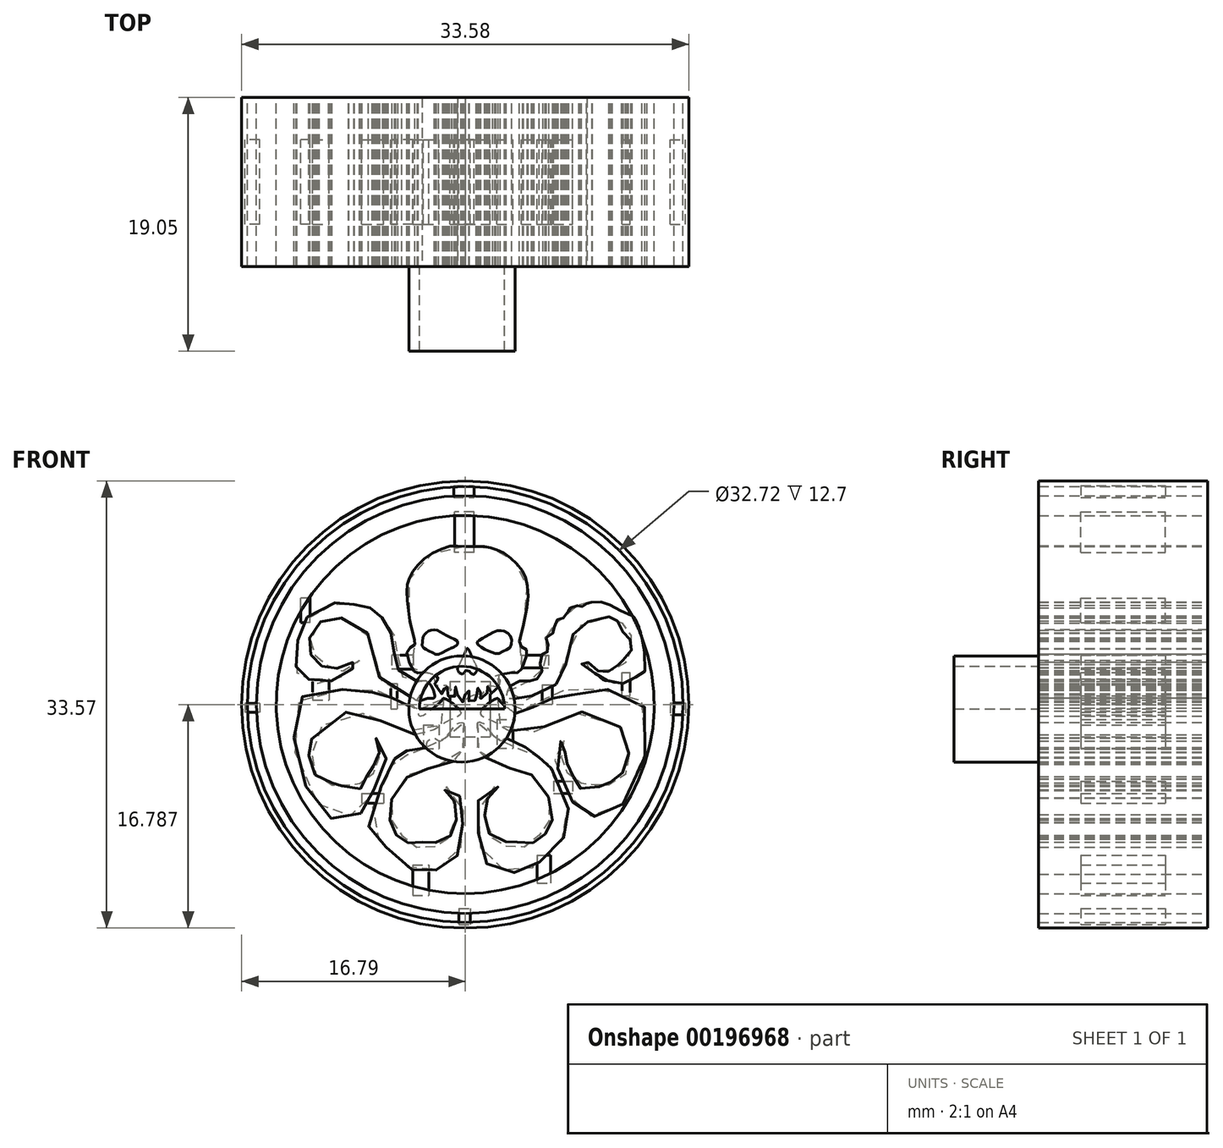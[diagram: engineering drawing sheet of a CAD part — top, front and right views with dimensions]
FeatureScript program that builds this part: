
annotation { "Feature Type Name" : "Feature", "Feature Type Description" : "" }
export const myFeature = defineFeature(function(context is Context, id is Id, definition is map)
    precondition{}
    {
        {
            var Q0;
            Q0=qCreatedBy(makeId("Front.planeOp"),FACE);
            var sketch = newSketch(context, id + "F0", { "sketchPlane" : qUnion([Q0])});
            skCircle(sketch, "E0", {"center": v(0.24, 0.34) * mm, "radius": 14.2 * mm});
            skCircle(sketch, "E1", {"center": v(0.24, 0.34) * mm, "radius": 15.68 * mm});
            skCircle(sketch, "E2", {"center": v(0.24, 0.34) * mm, "radius": 16.79 * mm});
            skCircle(sketch, "E3", {"center": v(0.24, 0.34) * mm, "radius": 16.36 * mm});
            skFitSpline(sketch, "E4", {"points": [v(0.24, 12.2) * mm, v(-0.86, 12.23) * mm, v(-2.49, 11.52) * mm, v(-3.6, 10.47) * mm, v(-4.06, 9.5) * mm, v(-4.12, 8.58) * mm, v(-3.9, 6.56) * mm, v(-3.64, 5.47) * mm, v(-3.58, 5.15) * mm, v(-3.58, 4.8) * mm, v(-4.12, 4.38) * mm, v(-3.55, 2.78) * mm, v(-3.29, 2.72) * mm, v(-2.58, 2.72) * mm, v(-2.06, 2.57) * mm, v(-1.85, 2.46) * mm, v(-1.75, 2.3) * mm, v(-2.04, 2.17) * mm, v(-1.82, 1.47) * mm, v(-1.34, 1.12) * mm, v(-1.27, 1.79) * mm, v(-1.14, 1.72) * mm, v(-1.11, 1.08) * mm, v(-0.58, 0.8) * mm, v(-0.56, 1.6) * mm, v(-0.35, 1.63) * mm, v(-0.33, 0.8) * mm, v(0.24, 0.58) * mm, v(0.24, 1.37) * mm, v(0.53, 1.37) * mm, v(0.53, 0.58) * mm, v(0.7, 0.58) * mm, v(1.14, 0.72) * mm, v(1.11, 1.02) * mm, v(1.14, 1.53) * mm, v(1.36, 1.57) * mm, v(1.38, 1.29) * mm, v(1.34, 0.8) * mm, v(1.84, 1.04) * mm, v(1.88, 1.47) * mm, v(1.92, 1.69) * mm, v(2.06, 1.77) * mm, v(2.02, 1.23) * mm, v(2.14, 1.16) * mm, v(2.55, 1.37) * mm, v(2.84, 2.2) * mm, v(2.53, 2.23) * mm, v(2.47, 2.38) * mm, v(2.6, 2.5) * mm, v(3.76, 2.74) * mm, v(4.1, 2.72) * mm, v(4.36, 2.79) * mm, v(4.9, 4.41) * mm, v(4.79, 4.45) * mm, v(4.38, 4.8) * mm, v(4.32, 5.16) * mm, v(4.5, 5.89) * mm, v(4.7, 6.75) * mm, v(4.95, 8.35) * mm, v(4.87, 9.56) * mm, v(4.58, 10.28) * mm, v(4, 11.03) * mm, v(3.25, 11.63) * mm, v(2.63, 11.96) * mm, v(2.06, 12.12) * mm, v(1.5, 12.2) * mm, v(0.24, 12.2) * mm]});
            skFitSpline(sketch, "E5", {"points": [v(-0.33, 5.1) * mm, v(-0.8, 5.34) * mm, v(-1.34, 5.62) * mm, v(-1.6, 5.78) * mm, v(-1.92, 5.92) * mm, v(-2.27, 5.94) * mm, v(-2.53, 5.84) * mm, v(-2.7, 5.7) * mm, v(-2.87, 5.5) * mm, v(-2.96, 5.2) * mm, v(-2.96, 4.65) * mm, v(-2.81, 4.55) * mm, v(-2.6, 4.43) * mm, v(-2.13, 4.19) * mm, v(-1.88, 4.09) * mm, v(-1.38, 4.27) * mm, v(-0.94, 4.53) * mm], "startDerivative": vector(-5.86, 3.13) * mm, "endDerivative": vector(5.52, 3.48) * mm});
            skFitSpline(sketch, "E6", {"points": [v(-0.94, 4.53) * mm, v(-0.7, 4.62) * mm, v(-0.43, 4.77) * mm, v(-0.34, 4.89) * mm, v(-0.33, 4.99) * mm, v(-0.33, 5.1) * mm], "startDerivative": vector(0.91, 0.3) * mm, "endDerivative": vector(0, 0.7) * mm});
            skFitSpline(sketch, "E7", {"points": [v(2.95, 5.9) * mm, v(2.67, 5.89) * mm, v(2.37, 5.75) * mm, v(2.08, 5.62) * mm, v(1.8, 5.46) * mm, v(1.6, 5.34) * mm, v(1.4, 5.23) * mm, v(1.23, 5.1) * mm, v(1.14, 5.04) * mm, v(1.14, 4.9) * mm, v(1.25, 4.8) * mm, v(1.48, 4.62) * mm, v(1.72, 4.47) * mm, v(1.97, 4.37) * mm, v(2.2, 4.3) * mm, v(2.43, 4.21) * mm, v(2.6, 4.14) * mm, v(2.86, 4.2) * mm, v(3.16, 4.36) * mm, v(3.45, 4.5) * mm, v(3.63, 4.65) * mm, v(3.7, 4.82) * mm, v(3.72, 5.12) * mm, v(3.68, 5.42) * mm, v(3.53, 5.6) * mm, v(3.33, 5.78) * mm, v(3.06, 5.88) * mm, v(2.95, 5.9) * mm]});
            skFitSpline(sketch, "E8", {"points": [v(0.39, 4.55) * mm, v(0.24, 4.26) * mm, v(-0.01, 3.77) * mm, v(-0.2, 3.37) * mm, v(-0.33, 3.01) * mm, v(-0.26, 2.82) * mm, v(-0.2, 2.71) * mm, v(-0.08, 2.65) * mm, v(-0.02, 2.62) * mm, v(0.24, 2.8) * mm, v(0.24, 2.87) * mm, v(0.5, 2.86) * mm, v(0.63, 2.74) * mm, v(0.73, 2.64) * mm, v(0.84, 2.6) * mm, v(1.08, 2.8) * mm, v(1.14, 2.95) * mm, v(1.13, 3.1) * mm, v(0.98, 3.45) * mm, v(0.8, 3.78) * mm, v(0.61, 4.24) * mm, v(0.39, 4.55) * mm]});
            skFitSpline(sketch, "E9", {"points": [v(-2.58, 2.06) * mm, v(-2.07, 0.87) * mm, v(-2.53, 0.8) * mm, v(-3.29, 0.61) * mm, v(-3.77, 0.87) * mm, v(-5.32, 1.53) * mm, v(-5.88, 1.94) * mm, v(-6.26, 2.52) * mm, v(-6.7, 4.27) * mm, v(-7.1, 5.7) * mm, v(-7.6, 6.26) * mm, v(-8.24, 6.59) * mm, v(-8.8, 6.79) * mm, v(-9.85, 6.9) * mm, v(-9.8, 6.74) * mm, v(-10.28, 6.45) * mm, v(-10.44, 6.61) * mm, v(-10.84, 6.3) * mm, v(-10.72, 6.1) * mm, v(-10.9, 5.7) * mm, v(-11.28, 5.7) * mm, v(-11.44, 5.23) * mm, v(-11.21, 5.2) * mm, v(-11.17, 4.7) * mm, v(-11.42, 4.55) * mm, v(-11.38, 4.1) * mm, v(-11.11, 4.1) * mm, v(-10.8, 3.68) * mm, v(-10.98, 3.49) * mm, v(-10.63, 3.1) * mm, v(-10.44, 3.32) * mm, v(-10, 3.16) * mm, v(-10, 2.85) * mm, v(-9.57, 2.83) * mm, v(-9.46, 3) * mm, v(-9.08, 3.04) * mm, v(-8.91, 2.85) * mm, v(-8.5, 3.07) * mm, v(-8.5, 3.26) * mm, v(-8.17, 3.5) * mm, v(-8.07, 3.49) * mm, v(-7.87, 3.63) * mm, v(-7.63, 3.6) * mm, v(-7.92, 3.14) * mm, v(-8.12, 3.07) * mm, v(-8.67, 2.72) * mm, v(-9.12, 2.38) * mm, v(-9.34, 2.2) * mm, v(-9.71, 2.11) * mm, v(-10.23, 2) * mm, v(-10.7, 1.92) * mm, v(-10.9, 1.91) * mm, v(-11.38, 2.14) * mm, v(-11.66, 2.32) * mm, v(-12.04, 2.52) * mm, v(-12.28, 2.61) * mm, v(-12.38, 2.72) * mm, v(-12.44, 2.83) * mm, v(-12.43, 3.47) * mm, v(-12.42, 4.27) * mm, v(-12.4, 4.55) * mm, v(-12.4, 4.88) * mm, v(-12.22, 5.43) * mm, v(-12.04, 6.04) * mm, v(-11.89, 6.44) * mm, v(-11.73, 6.78) * mm, v(-11.52, 6.98) * mm, v(-10.7, 7.35) * mm, v(-9.9, 7.77) * mm, v(-9.4, 8.02) * mm, v(-8.8, 8.02) * mm, v(-8.4, 8.02) * mm, v(-8.19, 8) * mm, v(-8.07, 7.92) * mm, v(-8.1, 7.85) * mm, v(-7.84, 7.74) * mm, v(-7.72, 7.64) * mm, v(-7.54, 7.6) * mm, v(-7.34, 7.8) * mm, v(-6.98, 7.64) * mm, v(-6.79, 7.55) * mm, v(-6.71, 7.48) * mm, v(-6.7, 7.39) * mm, v(-6.71, 7.21) * mm, v(-6.3, 6.84) * mm, v(-6.07, 6.9) * mm, v(-5.8, 6.6) * mm, v(-5.6, 6.23) * mm, v(-5.77, 6.08) * mm, v(-5.57, 5.7) * mm, v(-5.24, 5.7) * mm, v(-4.97, 4.99) * mm, v(-5.12, 4.86) * mm, v(-5.26, 4.66) * mm, v(-5.12, 4.27) * mm, v(-5.04, 4.12) * mm, v(-4.73, 4.1) * mm, v(-4.53, 3.5) * mm, v(-4.78, 3.17) * mm, v(-4.68, 2.72) * mm, v(-4.43, 2.36) * mm, v(-4.22, 2.1) * mm, v(-3.78, 2.11) * mm, v(-3.18, 2.09) * mm, v(-2.58, 2.06) * mm]});
            skFitSpline(sketch, "E10", {"points": [v(-1.38, 0.8) * mm, v(-0.33, 0.1) * mm, v(-0.13, -0.42) * mm, v(-1.11, -0.93) * mm, v(-1.82, -1.39) * mm, v(-2.58, -1.71) * mm, v(-3.18, -1.84) * mm, v(-3.55, -1.93) * mm, v(-4.08, -1.75) * mm, v(-5.14, -1.23) * mm, v(-5.95, -0.96) * mm, v(-6.83, -0.58) * mm, v(-7.63, -0.27) * mm, v(-8.1, -0.15) * mm, v(-9.15, -0.36) * mm, v(-10.12, -0.88) * mm, v(-10.98, -1.82) * mm, v(-11.41, -2.52) * mm, v(-11.28, -2.62) * mm, v(-11.23, -2.93) * mm, v(-11.23, -3.23) * mm, v(-11.26, -3.34) * mm, v(-11.43, -3.44) * mm, v(-11.5, -3.47) * mm, v(-11.37, -4.15) * mm, v(-11.17, -4.1) * mm, v(-10.81, -4.64) * mm, v(-10.77, -4.79) * mm, v(-11.02, -4.94) * mm, v(-10.72, -5.36) * mm, v(-10.5, -5.53) * mm, v(-10.28, -5.28) * mm, v(-9.97, -5.41) * mm, v(-9.86, -5.49) * mm, v(-9.77, -5.54) * mm, v(-9.77, -5.8) * mm, v(-9.74, -5.98) * mm, v(-9.38, -6.05) * mm, v(-9.21, -6.09) * mm, v(-9.1, -6.1) * mm, v(-9.05, -5.9) * mm, v(-9, -5.74) * mm, v(-8.75, -5.7) * mm, v(-8.58, -5.72) * mm, v(-8.45, -5.73) * mm, v(-8.28, -5.88) * mm, v(-8.2, -6.02) * mm, v(-7.63, -5.98) * mm, v(-7.63, -5.88) * mm, v(-7.52, -5.76) * mm, v(-7.63, -5.64) * mm, v(-7.69, -5.5) * mm, v(-7.63, -5.35) * mm, v(-7.32, -5.15) * mm, v(-7.2, -5.07) * mm, v(-7.11, -5.08) * mm, v(-6.94, -5.22) * mm, v(-6.8, -5.2) * mm, v(-6.73, -4.9) * mm, v(-6.6, -4.75) * mm, v(-6.73, -4.52) * mm, v(-6.63, -4.26) * mm, v(-6.6, -4.1) * mm, v(-6.58, -4.04) * mm, v(-6.53, -3.99) * mm, v(-6.39, -3.96) * mm, v(-6.22, -3.95) * mm, v(-6.21, -3.54) * mm, v(-6.19, -3.35) * mm, v(-6.24, -3.24) * mm, v(-6.43, -3.26) * mm, v(-6.5, -2.92) * mm, v(-6.52, -2.72) * mm, v(-6.45, -2.58) * mm, v(-6.35, -2.5) * mm, v(-6.38, -2.37) * mm, v(-6.45, -2.15) * mm, v(-6.17, -2.37) * mm, v(-5.96, -2.84) * mm, v(-5.82, -3.2) * mm, v(-5.72, -3.48) * mm, v(-5.72, -3.9) * mm, v(-5.9, -4.43) * mm, v(-6.19, -5.04) * mm, v(-6.53, -5.86) * mm, v(-6.76, -6.42) * mm, v(-7.05, -7.03) * mm, v(-7.3, -7.53) * mm, v(-7.42, -7.8) * mm, v(-7.63, -7.85) * mm, v(-8.07, -7.94) * mm, v(-8.78, -8.08) * mm, v(-9.43, -8.16) * mm, v(-9.8, -8.2) * mm, v(-10.18, -7.93) * mm, v(-10.8, -7.14) * mm, v(-11.64, -5.97) * mm, v(-12.1, -4.85) * mm, v(-12.57, -3) * mm, v(-12.62, -1.78) * mm, v(-12.6, -0.46) * mm, v(-12.22, 0.61) * mm, v(-11.76, 1.08) * mm, v(-10.81, 1.37) * mm, v(-9.38, 1.47) * mm, v(-8.68, 1.47) * mm, v(-7.63, 1.37) * mm, v(-7.3, 1.16) * mm, v(-6.83, 1.08) * mm, v(-6.6, 1.37) * mm, v(-5.93, 1.16) * mm, v(-5.96, 0.87) * mm, v(-5.8, 0.87) * mm, v(-5.56, 0.8) * mm, v(-5.3, 0.87) * mm, v(-4.94, 0.87) * mm, v(-4.69, 0.5) * mm, v(-4.55, 0.34) * mm, v(-4.2, 0.12) * mm, v(-4.08, 0.1) * mm, v(-3.89, 0.34) * mm, v(-3.55, 0.13) * mm, v(-3.29, -0.07) * mm, v(-3.29, -0.42) * mm, v(-3.09, -0.52) * mm, v(-2.4, -0.1) * mm, v(-1.55, 0.61) * mm, v(-1.38, 0.8) * mm]});
            skFitSpline(sketch, "E11", {"points": [v(0.1, -1.03) * mm, v(0.09, -1.74) * mm, v(0.12, -2.24) * mm, v(0.12, -2.77) * mm, v(0.12, -3) * mm, v(-0.37, -3.54) * mm, v(-0.75, -4.05) * mm, v(-1.5, -4.3) * mm, v(-2.18, -4.42) * mm, v(-2.72, -4.5) * mm, v(-3.2, -4.64) * mm, v(-3.68, -4.74) * mm, v(-3.93, -4.94) * mm, v(-4.46, -5.43) * mm, v(-4.79, -5.9) * mm, v(-5.15, -6.46) * mm, v(-5.36, -7) * mm, v(-5.46, -7.57) * mm, v(-5.49, -8.06) * mm, v(-5.5, -8.34) * mm, v(-5.3, -8.34) * mm, v(-5.2, -8.52) * mm, v(-5, -8.83) * mm, v(-5.03, -9.03) * mm, v(-5.06, -9.19) * mm, v(-4.73, -9.66) * mm, v(-4.5, -9.49) * mm, v(-4.26, -9.61) * mm, v(-3.96, -9.8) * mm, v(-4.03, -10.11) * mm, v(-3.66, -10.26) * mm, v(-3.48, -10.36) * mm, v(-3.36, -10.33) * mm, v(-3.32, -10.09) * mm, v(-2.68, -10.06) * mm, v(-2.53, -10.33) * mm, v(-2.18, -10.34) * mm, v(-1.95, -10.26) * mm, v(-1.96, -10.06) * mm, v(-2.02, -9.93) * mm, v(-1.54, -9.56) * mm, v(-1.32, -9.63) * mm, v(-1.2, -9.77) * mm, v(-0.77, -9.34) * mm, v(-1, -9.13) * mm, v(-0.8, -8.52) * mm, v(-0.52, -8.53) * mm, v(-0.45, -7.93) * mm, v(-0.62, -7.93) * mm, v(-0.7, -7.43) * mm, v(-0.55, -7.15) * mm, v(-0.6, -6.85) * mm, v(-0.7, -6.68) * mm, v(-0.88, -6.68) * mm, v(-1.15, -6.55) * mm, v(-1.3, -6.22) * mm, v(-1.3, -6.05) * mm, v(-1.44, -5.8) * mm, v(-0.67, -6.06) * mm, v(-0.28, -6.45) * mm, v(0.02, -6.76) * mm, v(0.1, -7.46) * mm, v(0.06, -8.33) * mm, v(0.06, -9.27) * mm, v(0.02, -9.97) * mm, v(-0.4, -11.15) * mm, v(-0.64, -11.68) * mm, v(-1.3, -11.87) * mm, v(-2.02, -12.12) * mm, v(-2.7, -12.31) * mm, v(-3.1, -12.41) * mm, v(-3.68, -12.14) * mm, v(-4.53, -11.5) * mm, v(-5.22, -10.83) * mm, v(-6.04, -10.06) * mm, v(-6.53, -9.43) * mm, v(-6.9, -8.97) * mm, v(-7.01, -8.77) * mm, v(-6.56, -7.02) * mm, v(-6.03, -5.68) * mm, v(-5.33, -4.32) * mm, v(-5.06, -3.92) * mm, v(-5.06, -3.75) * mm, v(-4.83, -3.6) * mm, v(-4.63, -3.68) * mm, v(-4.4, -3.57) * mm, v(-4.12, -3.45) * mm, v(-4.15, -3.05) * mm, v(-3.86, -2.97) * mm, v(-3.55, -2.87) * mm, v(-3.23, -2.97) * mm, v(-2.7, -2.88) * mm, v(-2.6, -2.41) * mm, v(-1.98, -2.21) * mm, v(-1.7, -2.41) * mm, v(-1.38, -2.25) * mm, v(-1.04, -1.93) * mm, v(-0.65, -1.4) * mm, v(-0.5, -1.2) * mm, v(-0.27, -1.07) * mm, v(0.1, -1.03) * mm]});
            skFitSpline(sketch, "E12.MirrorC", {"points": [v(0.1, -1.03) * mm, v(0.09, -1.74) * mm, v(0.12, -2.24) * mm, v(0.12, -2.77) * mm, v(0.12, -3) * mm, v(-0.37, -3.54) * mm, v(-0.75, -4.05) * mm, v(-1.5, -4.3) * mm, v(-2.18, -4.42) * mm, v(-2.72, -4.5) * mm, v(-3.2, -4.64) * mm, v(-3.68, -4.74) * mm, v(-3.93, -4.94) * mm, v(-4.46, -5.43) * mm, v(-4.79, -5.9) * mm, v(-5.15, -6.46) * mm, v(-5.36, -7) * mm, v(-5.46, -7.57) * mm, v(-5.49, -8.06) * mm, v(-5.5, -8.34) * mm, v(-5.3, -8.34) * mm, v(-5.2, -8.52) * mm, v(-5, -8.83) * mm, v(-5.03, -9.03) * mm, v(-5.06, -9.19) * mm, v(-4.73, -9.66) * mm, v(-4.5, -9.49) * mm, v(-4.26, -9.61) * mm, v(-3.96, -9.8) * mm, v(-4.03, -10.11) * mm, v(-3.66, -10.26) * mm, v(-3.48, -10.36) * mm, v(-3.36, -10.33) * mm, v(-3.32, -10.09) * mm, v(-2.68, -10.06) * mm, v(-2.53, -10.33) * mm, v(-2.18, -10.34) * mm, v(-1.95, -10.26) * mm, v(-1.96, -10.06) * mm, v(-2.02, -9.93) * mm, v(-1.54, -9.56) * mm, v(-1.32, -9.63) * mm, v(-1.2, -9.77) * mm, v(-0.77, -9.34) * mm, v(-1, -9.13) * mm, v(-0.8, -8.52) * mm, v(-0.52, -8.53) * mm, v(-0.45, -7.93) * mm, v(-0.62, -7.93) * mm, v(-0.7, -7.43) * mm, v(-0.55, -7.15) * mm, v(-0.6, -6.85) * mm, v(-0.7, -6.68) * mm, v(-0.88, -6.68) * mm, v(-1.15, -6.55) * mm, v(-1.3, -6.22) * mm, v(-1.3, -6.05) * mm, v(-1.44, -5.8) * mm, v(-0.67, -6.06) * mm, v(-0.28, -6.45) * mm, v(0.02, -6.76) * mm, v(0.1, -7.46) * mm, v(0.06, -8.33) * mm, v(0.06, -9.27) * mm, v(0.02, -9.97) * mm, v(-0.4, -11.15) * mm, v(-0.64, -11.68) * mm, v(-1.3, -11.87) * mm, v(-2.02, -12.12) * mm, v(-2.7, -12.31) * mm, v(-3.1, -12.41) * mm, v(-3.68, -12.14) * mm, v(-4.53, -11.5) * mm, v(-5.22, -10.83) * mm, v(-6.04, -10.06) * mm, v(-6.53, -9.43) * mm, v(-6.9, -8.97) * mm, v(-7.01, -8.77) * mm, v(-6.56, -7.02) * mm, v(-6.03, -5.68) * mm, v(-5.33, -4.32) * mm, v(-5.06, -3.92) * mm, v(-5.06, -3.75) * mm, v(-4.83, -3.6) * mm, v(-4.63, -3.68) * mm, v(-4.4, -3.57) * mm, v(-4.12, -3.45) * mm, v(-4.15, -3.05) * mm, v(-3.86, -2.97) * mm, v(-3.55, -2.87) * mm, v(-3.23, -2.97) * mm, v(-2.7, -2.88) * mm, v(-2.6, -2.41) * mm, v(-1.98, -2.21) * mm, v(-1.7, -2.41) * mm, v(-1.38, -2.25) * mm, v(-1.04, -1.93) * mm, v(-0.65, -1.4) * mm, v(-0.5, -1.2) * mm, v(-0.27, -1.07) * mm, v(0.1, -1.03) * mm], "construction": true});
            skFitSpline(sketch, "E13.MirrorC", {"points": [v(1.17, -1.03) * mm, v(1.19, -1.74) * mm, v(1.16, -2.24) * mm, v(1.16, -2.77) * mm, v(1.16, -3) * mm, v(1.64, -3.54) * mm, v(2.03, -4.05) * mm, v(2.77, -4.3) * mm, v(3.45, -4.42) * mm, v(4, -4.5) * mm, v(4.47, -4.64) * mm, v(4.95, -4.74) * mm, v(5.2, -4.94) * mm, v(5.74, -5.43) * mm, v(6.06, -5.9) * mm, v(6.42, -6.46) * mm, v(6.64, -7) * mm, v(6.74, -7.57) * mm, v(6.76, -8.06) * mm, v(6.78, -8.34) * mm, v(6.58, -8.34) * mm, v(6.48, -8.52) * mm, v(6.28, -8.83) * mm, v(6.3, -9.03) * mm, v(6.34, -9.19) * mm, v(6, -9.66) * mm, v(5.78, -9.49) * mm, v(5.54, -9.61) * mm, v(5.24, -9.8) * mm, v(5.3, -10.11) * mm, v(4.94, -10.26) * mm, v(4.75, -10.36) * mm, v(4.64, -10.33) * mm, v(4.6, -10.09) * mm, v(3.95, -10.06) * mm, v(3.81, -10.33) * mm, v(3.45, -10.34) * mm, v(3.23, -10.26) * mm, v(3.24, -10.06) * mm, v(3.3, -9.93) * mm, v(2.81, -9.56) * mm, v(2.6, -9.63) * mm, v(2.47, -9.77) * mm, v(2.04, -9.34) * mm, v(2.28, -9.13) * mm, v(2.07, -8.52) * mm, v(1.8, -8.53) * mm, v(1.73, -7.93) * mm, v(1.9, -7.93) * mm, v(1.99, -7.43) * mm, v(1.83, -7.15) * mm, v(1.87, -6.85) * mm, v(1.99, -6.68) * mm, v(2.16, -6.68) * mm, v(2.43, -6.55) * mm, v(2.57, -6.22) * mm, v(2.58, -6.05) * mm, v(2.71, -5.8) * mm, v(1.94, -6.06) * mm, v(1.56, -6.45) * mm, v(1.26, -6.76) * mm, v(1.17, -7.46) * mm, v(1.22, -8.33) * mm, v(1.22, -9.27) * mm, v(1.26, -9.97) * mm, v(1.67, -11.15) * mm, v(1.91, -11.68) * mm, v(2.57, -11.87) * mm, v(3.3, -12.12) * mm, v(3.97, -12.31) * mm, v(4.38, -12.41) * mm, v(4.95, -12.14) * mm, v(5.8, -11.5) * mm, v(6.5, -10.83) * mm, v(7.32, -10.06) * mm, v(7.8, -9.43) * mm, v(8.18, -8.97) * mm, v(8.3, -8.77) * mm, v(7.83, -7.02) * mm, v(7.3, -5.68) * mm, v(6.6, -4.32) * mm, v(6.34, -3.92) * mm, v(6.34, -3.75) * mm, v(6.1, -3.6) * mm, v(5.9, -3.68) * mm, v(5.68, -3.57) * mm, v(5.4, -3.45) * mm, v(5.42, -3.05) * mm, v(5.14, -2.97) * mm, v(4.82, -2.87) * mm, v(4.5, -2.97) * mm, v(3.98, -2.88) * mm, v(3.87, -2.41) * mm, v(3.25, -2.21) * mm, v(2.98, -2.41) * mm, v(2.66, -2.25) * mm, v(2.31, -1.93) * mm, v(1.93, -1.4) * mm, v(1.79, -1.2) * mm, v(1.54, -1.07) * mm, v(1.17, -1.03) * mm]});
            skFitSpline(sketch, "E14.MirrorC", {"points": [v(2.66, 0.8) * mm, v(1.6, 0.1) * mm, v(1.4, -0.42) * mm, v(2.39, -0.93) * mm, v(3.1, -1.39) * mm, v(3.86, -1.71) * mm, v(4.46, -1.84) * mm, v(4.82, -1.93) * mm, v(5.35, -1.75) * mm, v(6.41, -1.23) * mm, v(7.22, -0.96) * mm, v(8.11, -0.58) * mm, v(8.91, -0.27) * mm, v(9.38, -0.15) * mm, v(10.43, -0.36) * mm, v(11.4, -0.88) * mm, v(12.26, -1.82) * mm, v(12.69, -2.52) * mm, v(12.56, -2.62) * mm, v(12.5, -2.93) * mm, v(12.5, -3.23) * mm, v(12.53, -3.34) * mm, v(12.71, -3.44) * mm, v(12.77, -3.47) * mm, v(12.65, -4.15) * mm, v(12.44, -4.1) * mm, v(12.09, -4.64) * mm, v(12.05, -4.79) * mm, v(12.3, -4.94) * mm, v(12, -5.36) * mm, v(11.78, -5.53) * mm, v(11.55, -5.28) * mm, v(11.25, -5.41) * mm, v(11.13, -5.49) * mm, v(11.05, -5.54) * mm, v(11.05, -5.8) * mm, v(11.02, -5.98) * mm, v(10.65, -6.05) * mm, v(10.49, -6.09) * mm, v(10.37, -6.1) * mm, v(10.32, -5.9) * mm, v(10.28, -5.74) * mm, v(10.03, -5.7) * mm, v(9.85, -5.72) * mm, v(9.72, -5.73) * mm, v(9.56, -5.88) * mm, v(9.47, -6.02) * mm, v(8.91, -5.98) * mm, v(8.91, -5.88) * mm, v(8.8, -5.76) * mm, v(8.91, -5.64) * mm, v(8.96, -5.5) * mm, v(8.91, -5.35) * mm, v(8.6, -5.15) * mm, v(8.48, -5.07) * mm, v(8.4, -5.08) * mm, v(8.21, -5.22) * mm, v(8.09, -5.2) * mm, v(8, -4.9) * mm, v(7.88, -4.75) * mm, v(8, -4.52) * mm, v(7.9, -4.26) * mm, v(7.88, -4.1) * mm, v(7.86, -4.04) * mm, v(7.8, -3.99) * mm, v(7.67, -3.96) * mm, v(7.5, -3.95) * mm, v(7.49, -3.54) * mm, v(7.46, -3.35) * mm, v(7.51, -3.24) * mm, v(7.7, -3.26) * mm, v(7.78, -2.92) * mm, v(7.8, -2.72) * mm, v(7.73, -2.58) * mm, v(7.63, -2.5) * mm, v(7.65, -2.37) * mm, v(7.73, -2.15) * mm, v(7.45, -2.37) * mm, v(7.23, -2.84) * mm, v(7.1, -3.2) * mm, v(7, -3.48) * mm, v(7, -3.9) * mm, v(7.18, -4.43) * mm, v(7.46, -5.04) * mm, v(7.8, -5.86) * mm, v(8.03, -6.42) * mm, v(8.33, -7.03) * mm, v(8.58, -7.53) * mm, v(8.7, -7.8) * mm, v(8.91, -7.85) * mm, v(9.34, -7.94) * mm, v(10.05, -8.08) * mm, v(10.7, -8.16) * mm, v(11.08, -8.2) * mm, v(11.45, -7.93) * mm, v(12.08, -7.14) * mm, v(12.91, -5.97) * mm, v(13.38, -4.85) * mm, v(13.84, -3) * mm, v(13.9, -1.78) * mm, v(13.87, -0.46) * mm, v(13.5, 0.61) * mm, v(13.04, 1.08) * mm, v(12.09, 1.37) * mm, v(10.65, 1.47) * mm, v(9.95, 1.47) * mm, v(8.91, 1.37) * mm, v(8.57, 1.16) * mm, v(8.11, 1.08) * mm, v(7.87, 1.37) * mm, v(7.2, 1.16) * mm, v(7.23, 0.87) * mm, v(7.07, 0.87) * mm, v(6.84, 0.8) * mm, v(6.57, 0.87) * mm, v(6.22, 0.87) * mm, v(5.96, 0.5) * mm, v(5.83, 0.34) * mm, v(5.48, 0.12) * mm, v(5.35, 0.1) * mm, v(5.16, 0.34) * mm, v(4.82, 0.13) * mm, v(4.57, -0.07) * mm, v(4.57, -0.42) * mm, v(4.36, -0.52) * mm, v(3.68, -0.1) * mm, v(2.82, 0.61) * mm, v(2.66, 0.8) * mm]});
            skFitSpline(sketch, "E15.MirrorC", {"points": [v(3.86, 2.06) * mm, v(3.35, 0.87) * mm, v(3.81, 0.8) * mm, v(4.57, 0.61) * mm, v(5.05, 0.87) * mm, v(6.6, 1.53) * mm, v(7.16, 1.94) * mm, v(7.54, 2.52) * mm, v(7.97, 4.27) * mm, v(8.38, 5.7) * mm, v(8.89, 6.26) * mm, v(9.52, 6.59) * mm, v(10.08, 6.79) * mm, v(11.12, 6.9) * mm, v(11.08, 6.74) * mm, v(11.56, 6.45) * mm, v(11.71, 6.61) * mm, v(12.12, 6.3) * mm, v(12, 6.1) * mm, v(12.18, 5.7) * mm, v(12.55, 5.7) * mm, v(12.72, 5.23) * mm, v(12.49, 5.2) * mm, v(12.45, 4.7) * mm, v(12.7, 4.55) * mm, v(12.65, 4.1) * mm, v(12.39, 4.1) * mm, v(12.08, 3.68) * mm, v(12.26, 3.49) * mm, v(11.9, 3.1) * mm, v(11.71, 3.32) * mm, v(11.27, 3.16) * mm, v(11.28, 2.85) * mm, v(10.85, 2.83) * mm, v(10.73, 3) * mm, v(10.35, 3.04) * mm, v(10.19, 2.85) * mm, v(9.78, 3.07) * mm, v(9.78, 3.26) * mm, v(9.45, 3.5) * mm, v(9.35, 3.49) * mm, v(9.15, 3.63) * mm, v(8.91, 3.6) * mm, v(9.2, 3.14) * mm, v(9.4, 3.07) * mm, v(9.95, 2.72) * mm, v(10.4, 2.38) * mm, v(10.62, 2.2) * mm, v(10.99, 2.11) * mm, v(11.5, 2) * mm, v(11.98, 1.92) * mm, v(12.18, 1.91) * mm, v(12.65, 2.14) * mm, v(12.93, 2.32) * mm, v(13.31, 2.52) * mm, v(13.56, 2.61) * mm, v(13.66, 2.72) * mm, v(13.72, 2.83) * mm, v(13.7, 3.47) * mm, v(13.7, 4.27) * mm, v(13.68, 4.55) * mm, v(13.67, 4.88) * mm, v(13.5, 5.43) * mm, v(13.31, 6.04) * mm, v(13.16, 6.44) * mm, v(13, 6.78) * mm, v(12.8, 6.98) * mm, v(11.97, 7.35) * mm, v(11.17, 7.77) * mm, v(10.68, 8.02) * mm, v(10.07, 8.02) * mm, v(9.67, 8.02) * mm, v(9.46, 8) * mm, v(9.35, 7.92) * mm, v(9.37, 7.85) * mm, v(9.12, 7.74) * mm, v(9, 7.64) * mm, v(8.82, 7.6) * mm, v(8.61, 7.8) * mm, v(8.26, 7.64) * mm, v(8.07, 7.55) * mm, v(7.99, 7.48) * mm, v(7.98, 7.39) * mm, v(7.99, 7.21) * mm, v(7.58, 6.84) * mm, v(7.34, 6.9) * mm, v(7.07, 6.6) * mm, v(6.88, 6.23) * mm, v(7.05, 6.08) * mm, v(6.85, 5.7) * mm, v(6.52, 5.7) * mm, v(6.25, 4.99) * mm, v(6.4, 4.86) * mm, v(6.54, 4.66) * mm, v(6.4, 4.27) * mm, v(6.31, 4.12) * mm, v(6, 4.1) * mm, v(5.8, 3.5) * mm, v(6.06, 3.17) * mm, v(5.96, 2.72) * mm, v(5.7, 2.36) * mm, v(5.5, 2.1) * mm, v(5.05, 2.11) * mm, v(4.46, 2.09) * mm, v(3.86, 2.06) * mm]});
            skSolve(sketch);
        }
        {
            var Q0;
            Q0=makeQuery(id+"F0.imprint","IMPRINT",FACE,{"disambiguationData":[TD([[makeQuery(id+"F0.imprint","IMPRINT",EDGE,{"derivedFrom":sQuery(id+"F0.wireOp",EDGE,"E4")}),1.0]])]});
            var Q1;
            Q1=makeQuery(id+"F0.imprint","IMPRINT",FACE,{"disambiguationData":[TD([[makeQuery(id+"F0.imprint","IMPRINT",EDGE,{"derivedFrom":sQuery(id+"F0.wireOp",EDGE,"E9")}),-1.0]])]});
            var Q2;
            {var subQ0=sQuery(id+"F0.wireOp",EDGE,"E15.MirrorC");var subQ1=sQuery(id+"F0.wireOp",EDGE,"E0");var subQ2=makeQuery(id+"F0.imprint","INTERSECT",VERTEX,{"disambiguationData":[OD(0.0)],"derivedFrom":[subQ1,subQ0]});Q2=makeQuery(id+"F0.imprint","IMPRINT",FACE,{"disambiguationData":[TD([[makeQuery(id+"F0.imprint","IMPRINT",EDGE,{"disambiguationData":[TD([[subQ2,1.0]])],"derivedFrom":subQ1}),1.0]])]});}
            var Q3;
            Q3=makeQuery(id+"F0.imprint","IMPRINT",FACE,{"disambiguationData":[TD([[makeQuery(id+"F0.imprint","IMPRINT",EDGE,{"derivedFrom":sQuery(id+"F0.wireOp",EDGE,"E14.MirrorC")}),1.0]])]});
            var Q4;
            Q4=makeQuery(id+"F0.imprint","IMPRINT",FACE,{"disambiguationData":[TD([[makeQuery(id+"F0.imprint","IMPRINT",EDGE,{"derivedFrom":sQuery(id+"F0.wireOp",EDGE,"E13.MirrorC")}),1.0]])]});
            var Q5;
            Q5=makeQuery(id+"F0.imprint","IMPRINT",FACE,{"disambiguationData":[TD([[makeQuery(id+"F0.imprint","IMPRINT",EDGE,{"derivedFrom":sQuery(id+"F0.wireOp",EDGE,"E11")}),-1.0]])]});
            var Q6;
            Q6=makeQuery(id+"F0.imprint","IMPRINT",FACE,{"disambiguationData":[TD([[makeQuery(id+"F0.imprint","IMPRINT",EDGE,{"derivedFrom":sQuery(id+"F0.wireOp",EDGE,"E10")}),-1.0]])]});
            var Q7;
            Q7=makeQuery(id+"F0.imprint","IMPRINT",FACE,{"disambiguationData":[TD([[makeQuery(id+"F0.imprint","IMPRINT",EDGE,{"derivedFrom":sQuery(id+"F0.wireOp",EDGE,"E1")}),1.0]])]});
            var Q8;
            Q8=makeQuery(id+"F0.imprint","IMPRINT",FACE,{"disambiguationData":[TD([[makeQuery(id+"F0.imprint","IMPRINT",EDGE,{"derivedFrom":sQuery(id+"F0.wireOp",EDGE,"E2")}),1.0]])]});
            extrude(context, id + "F1", {"entities" : qUnion([Q0, Q1, Q2, Q3, Q4, Q5, Q6, Q7, Q8]), "depth" : 12.7 * mm});
        }
        {
            var Q0;
            Q0=qCreatedBy(makeId("Front.planeOp"),FACE);
            cPlane(context, id + "F2", {"entities" : qUnion([Q0]), "cplaneType" : CPlaneType.OFFSET, "offset" : 6.35 * mm, "width" : 152.4 * mm, "height" : 152.4 * mm});
        }
        {
            var Q0;
            Q0=qCreatedBy(id+"F2.planeOp",FACE);
            var sketch = newSketch(context, id + "F3", { "sketchPlane" : qUnion([Q0])});
            skLineSegment(sketch, "E16.bottom", {"start": v(-0.63, 16.78) * mm, "end": v(0.9, 16.78) * mm});
            skLineSegment(sketch, "E16.top", {"start": v(-0.63, 15.89) * mm, "end": v(0.9, 15.89) * mm});
            skLineSegment(sketch, "E16.left", {"start": v(-0.63, 16.78) * mm, "end": v(-0.63, 15.89) * mm});
            skLineSegment(sketch, "E16.right", {"start": v(0.9, 16.78) * mm, "end": v(0.9, 15.89) * mm});
            skLineSegment(sketch, "E17.bottom", {"start": v(-15.2, 0.43) * mm, "end": v(-16.32, 0.43) * mm});
            skLineSegment(sketch, "E17.top", {"start": v(-15.2, -0.25) * mm, "end": v(-16.32, -0.25) * mm});
            skLineSegment(sketch, "E17.left", {"start": v(-15.2, 0.43) * mm, "end": v(-15.2, -0.25) * mm});
            skLineSegment(sketch, "E17.right", {"start": v(-16.32, 0.43) * mm, "end": v(-16.32, -0.25) * mm});
            skLineSegment(sketch, "E18.bottom", {"start": v(15.63, 0.44) * mm, "end": v(16.78, 0.44) * mm});
            skLineSegment(sketch, "E18.top", {"start": v(15.63, -0.43) * mm, "end": v(16.78, -0.43) * mm});
            skLineSegment(sketch, "E18.left", {"start": v(15.63, 0.44) * mm, "end": v(15.63, -0.43) * mm});
            skLineSegment(sketch, "E18.right", {"start": v(16.78, 0.44) * mm, "end": v(16.78, -0.43) * mm});
            skLineSegment(sketch, "E19.bottom", {"start": v(-0.23, -14.97) * mm, "end": v(0.6, -14.97) * mm});
            skLineSegment(sketch, "E19.top", {"start": v(-0.23, -16.19) * mm, "end": v(0.6, -16.19) * mm});
            skLineSegment(sketch, "E19.left", {"start": v(-0.23, -14.97) * mm, "end": v(-0.23, -16.19) * mm});
            skLineSegment(sketch, "E19.right", {"start": v(0.6, -14.97) * mm, "end": v(0.6, -16.19) * mm});
            skLineSegment(sketch, "E20.bottom", {"start": v(5.64, -10.99) * mm, "end": v(6.67, -10.99) * mm});
            skLineSegment(sketch, "E20.top", {"start": v(5.64, -13.07) * mm, "end": v(6.67, -13.07) * mm});
            skLineSegment(sketch, "E20.left", {"start": v(5.64, -10.99) * mm, "end": v(5.64, -13.07) * mm});
            skLineSegment(sketch, "E20.right", {"start": v(6.67, -10.99) * mm, "end": v(6.67, -13.07) * mm});
            skLineSegment(sketch, "E21.bottom", {"start": v(-3.7, -11.72) * mm, "end": v(-2.5, -11.72) * mm});
            skLineSegment(sketch, "E21.top", {"start": v(-3.7, -13.98) * mm, "end": v(-2.5, -13.98) * mm});
            skLineSegment(sketch, "E21.left", {"start": v(-3.7, -11.72) * mm, "end": v(-3.7, -13.98) * mm});
            skLineSegment(sketch, "E21.right", {"start": v(-2.5, -11.72) * mm, "end": v(-2.5, -13.98) * mm});
            skLineSegment(sketch, "E22.bottom", {"start": v(6.89, -5.44) * mm, "end": v(8.3, -5.44) * mm});
            skLineSegment(sketch, "E22.top", {"start": v(6.89, -6.35) * mm, "end": v(8.3, -6.35) * mm});
            skLineSegment(sketch, "E22.left", {"start": v(6.89, -5.44) * mm, "end": v(6.89, -6.35) * mm});
            skLineSegment(sketch, "E22.right", {"start": v(8.3, -5.44) * mm, "end": v(8.3, -6.35) * mm});
            skLineSegment(sketch, "E23.bottom", {"start": v(2.61, -0.8) * mm, "end": v(3.82, -0.8) * mm});
            skLineSegment(sketch, "E23.top", {"start": v(2.61, -2.95) * mm, "end": v(3.82, -2.95) * mm});
            skLineSegment(sketch, "E23.left", {"start": v(2.61, -0.8) * mm, "end": v(2.61, -2.95) * mm});
            skLineSegment(sketch, "E23.right", {"start": v(3.82, -0.8) * mm, "end": v(3.82, -2.95) * mm});
            skLineSegment(sketch, "E24.bottom", {"start": v(-2.9, -1.2) * mm, "end": v(-1.73, -1.2) * mm});
            skLineSegment(sketch, "E24.top", {"start": v(-2.9, -2.99) * mm, "end": v(-1.73, -2.99) * mm});
            skLineSegment(sketch, "E24.left", {"start": v(-2.9, -1.2) * mm, "end": v(-2.9, -2.99) * mm});
            skLineSegment(sketch, "E24.right", {"start": v(-1.73, -1.2) * mm, "end": v(-1.73, -2.99) * mm});
            skLineSegment(sketch, "E25.bottom", {"start": v(-0.9, 2.09) * mm, "end": v(2.12, 2.09) * mm});
            skLineSegment(sketch, "E25.top", {"start": v(-0.9, -2.09) * mm, "end": v(2.12, -2.09) * mm});
            skLineSegment(sketch, "E25.left", {"start": v(-0.9, 2.09) * mm, "end": v(-0.9, -2.09) * mm});
            skLineSegment(sketch, "E25.right", {"start": v(2.12, 2.09) * mm, "end": v(2.12, -2.09) * mm});
            skLineSegment(sketch, "E26.bottom", {"start": v(-7.54, -6.35) * mm, "end": v(-5.88, -6.35) * mm});
            skLineSegment(sketch, "E26.top", {"start": v(-7.54, -7.07) * mm, "end": v(-5.88, -7.07) * mm});
            skLineSegment(sketch, "E26.left", {"start": v(-7.54, -6.35) * mm, "end": v(-7.54, -7.07) * mm});
            skLineSegment(sketch, "E26.right", {"start": v(-5.88, -6.35) * mm, "end": v(-5.88, -7.07) * mm});
            skLineSegment(sketch, "E27.bottom", {"start": v(12.02, 1) * mm, "end": v(12.63, 1) * mm});
            skLineSegment(sketch, "E27.top", {"start": v(12.02, 2.72) * mm, "end": v(12.63, 2.72) * mm});
            skLineSegment(sketch, "E27.left", {"start": v(12.02, 1) * mm, "end": v(12.02, 2.72) * mm});
            skLineSegment(sketch, "E27.right", {"start": v(12.63, 1) * mm, "end": v(12.63, 2.72) * mm});
            skLineSegment(sketch, "E28.bottom", {"start": v(6.03, 1.81) * mm, "end": v(6.78, 1.81) * mm});
            skLineSegment(sketch, "E28.top", {"start": v(6.03, 0.35) * mm, "end": v(6.78, 0.35) * mm});
            skLineSegment(sketch, "E28.left", {"start": v(6.03, 1.81) * mm, "end": v(6.03, 0.35) * mm});
            skLineSegment(sketch, "E28.right", {"start": v(6.78, 1.81) * mm, "end": v(6.78, 0.35) * mm});
            skLineSegment(sketch, "E29.bottom", {"start": v(-5.36, 1.91) * mm, "end": v(-4.87, 1.91) * mm});
            skLineSegment(sketch, "E29.top", {"start": v(-5.36, 0) * mm, "end": v(-4.87, 0) * mm});
            skLineSegment(sketch, "E29.left", {"start": v(-5.36, 1.91) * mm, "end": v(-5.36, 0) * mm});
            skLineSegment(sketch, "E29.right", {"start": v(-4.87, 1.91) * mm, "end": v(-4.87, 0) * mm});
            skLineSegment(sketch, "E30.bottom", {"start": v(-11.21, 2.27) * mm, "end": v(-9.98, 2.27) * mm});
            skLineSegment(sketch, "E30.top", {"start": v(-11.21, 0.67) * mm, "end": v(-9.98, 0.67) * mm});
            skLineSegment(sketch, "E30.left", {"start": v(-11.21, 2.27) * mm, "end": v(-11.21, 0.67) * mm});
            skLineSegment(sketch, "E30.right", {"start": v(-9.98, 2.27) * mm, "end": v(-9.98, 0.67) * mm});
            skLineSegment(sketch, "E31.bottom", {"start": v(-3.67, 4.03) * mm, "end": v(-5.28, 4.03) * mm});
            skLineSegment(sketch, "E31.top", {"start": v(-3.67, 2.99) * mm, "end": v(-5.28, 2.99) * mm});
            skLineSegment(sketch, "E31.left", {"start": v(-3.67, 4.03) * mm, "end": v(-3.67, 2.99) * mm});
            skLineSegment(sketch, "E31.right", {"start": v(-5.28, 4.03) * mm, "end": v(-5.28, 2.99) * mm});
            skLineSegment(sketch, "E32.bottom", {"start": v(4.45, 4.03) * mm, "end": v(6.5, 4.03) * mm});
            skLineSegment(sketch, "E32.top", {"start": v(4.45, 3.07) * mm, "end": v(6.5, 3.07) * mm});
            skLineSegment(sketch, "E32.left", {"start": v(4.45, 4.03) * mm, "end": v(4.45, 3.07) * mm});
            skLineSegment(sketch, "E32.right", {"start": v(6.5, 4.03) * mm, "end": v(6.5, 3.07) * mm});
            skLineSegment(sketch, "E33.bottom", {"start": v(0.9, 11.75) * mm, "end": v(-0.54, 11.75) * mm});
            skLineSegment(sketch, "E33.top", {"start": v(0.9, 14.82) * mm, "end": v(-0.54, 14.82) * mm});
            skLineSegment(sketch, "E33.left", {"start": v(0.9, 11.75) * mm, "end": v(0.9, 14.82) * mm});
            skLineSegment(sketch, "E33.right", {"start": v(-0.54, 11.75) * mm, "end": v(-0.54, 14.82) * mm});
            skLineSegment(sketch, "E34.bottom", {"start": v(-11.41, 6.48) * mm, "end": v(-12.1, 6.48) * mm});
            skLineSegment(sketch, "E34.top", {"start": v(-11.41, 8.32) * mm, "end": v(-12.1, 8.32) * mm});
            skLineSegment(sketch, "E34.left", {"start": v(-11.41, 6.48) * mm, "end": v(-11.41, 8.32) * mm});
            skLineSegment(sketch, "E34.right", {"start": v(-12.1, 6.48) * mm, "end": v(-12.1, 8.32) * mm});
            skSolve(sketch);
        }
        {
            var Q0;
            Q0 = qSketchRegion(id + "F3", true);
            extrude(context, id + "F4", {"entities" : qUnion([Q0]), "endBound" : BoundingType.SYMMETRIC, "depth" : 6.35 * mm});
        }
        {
            var Q0;
            Q0=makeQuery(id+"F1.opExtrude","CAP_FACE",FACE,{"disambiguationData":[OSD([sQuery(id+"F0.wireOp",EDGE,"E4"),sQuery(id+"F0.wireOp",EDGE,"E5"),sQuery(id+"F0.wireOp",EDGE,"E6"),sQuery(id+"F0.wireOp",EDGE,"E7"),sQuery(id+"F0.wireOp",EDGE,"E8")])],"isStart":false});
            var sketch = newSketch(context, id + "F5", { "sketchPlane" : qUnion([Q0])});
            skArc(sketch, "E35", {"start": v(3.2, 0) * mm, "mid": v(0, 3.2) * mm, "end": v(-3.2, 0) * mm});
            skCircle(sketch, "E36", {"center": v(0, 0) * mm, "radius": 4 * mm});
            skLineSegment(sketch, "E37", {"start": v(-3.2, 0) * mm, "end": v(3.2, 0) * mm});
            skSolve(sketch);
        }
        {
            var Q0;
            {var subQ0=sQuery(id+"F5.wireOp",EDGE,"E37");Q0=makeQuery(id+"F5.imprint","IMPRINT",FACE,{"disambiguationData":[TD([[makeQuery(id+"F5.imprint","IMPRINT",EDGE,{"derivedFrom":subQ0}),-1.0]])]});}
            var Q1;
            {var subQ0=sQuery(id+"F5.wireOp",EDGE,"E35");var subQ1=makeQuery(id+"F1.opExtrude","CAP_EDGE",EDGE,{"disambiguationData":[OSD([sQuery(id+"F0.wireOp",EDGE,"E8")])],"isStart":false});var subQ2=makeQuery(id+"F5.imprint","INTERSECT",VERTEX,{"disambiguationData":[OD(1.0)],"derivedFrom":[subQ1,subQ0]});Q1=makeQuery(id+"F5.imprint","IMPRINT",FACE,{"disambiguationData":[TD([[makeQuery(id+"F5.imprint","IMPRINT",EDGE,{"disambiguationData":[TD([[subQ2,-1.0]])],"derivedFrom":subQ0}),-1.0]])]});}
            var Q2;
            {var subQ0=sQuery(id+"F5.wireOp",EDGE,"E35");var subQ1=makeQuery(id+"F1.opExtrude","CAP_EDGE",EDGE,{"disambiguationData":[OSD([sQuery(id+"F0.wireOp",EDGE,"E4")])],"isStart":false});var subQ2=makeQuery(id+"F5.imprint","INTERSECT",VERTEX,{"disambiguationData":[OD(0.0)],"derivedFrom":[subQ1,subQ0]});Q2=makeQuery(id+"F5.imprint","IMPRINT",FACE,{"disambiguationData":[TD([[makeQuery(id+"F5.imprint","IMPRINT",EDGE,{"disambiguationData":[TD([[subQ2,-1.0]])],"derivedFrom":subQ0}),-1.0]])]});}
            var Q3;
            {var subQ0=sQuery(id+"F5.wireOp",EDGE,"E35");var subQ1=makeQuery(id+"F1.opExtrude","CAP_EDGE",EDGE,{"disambiguationData":[OSD([sQuery(id+"F0.wireOp",EDGE,"E8")])],"isStart":false});var subQ2=makeQuery(id+"F5.imprint","INTERSECT",VERTEX,{"disambiguationData":[OD(0.0)],"derivedFrom":[subQ1,subQ0]});Q3=makeQuery(id+"F5.imprint","IMPRINT",FACE,{"disambiguationData":[TD([[makeQuery(id+"F5.imprint","IMPRINT",EDGE,{"disambiguationData":[TD([[subQ2,-1.0]])],"derivedFrom":subQ0}),-1.0]])]});}
            extrude(context, id + "F6", {"entities" : qUnion([Q0, Q1, Q2, Q3]), "depth" : 6.35 * mm});
        }
    });
